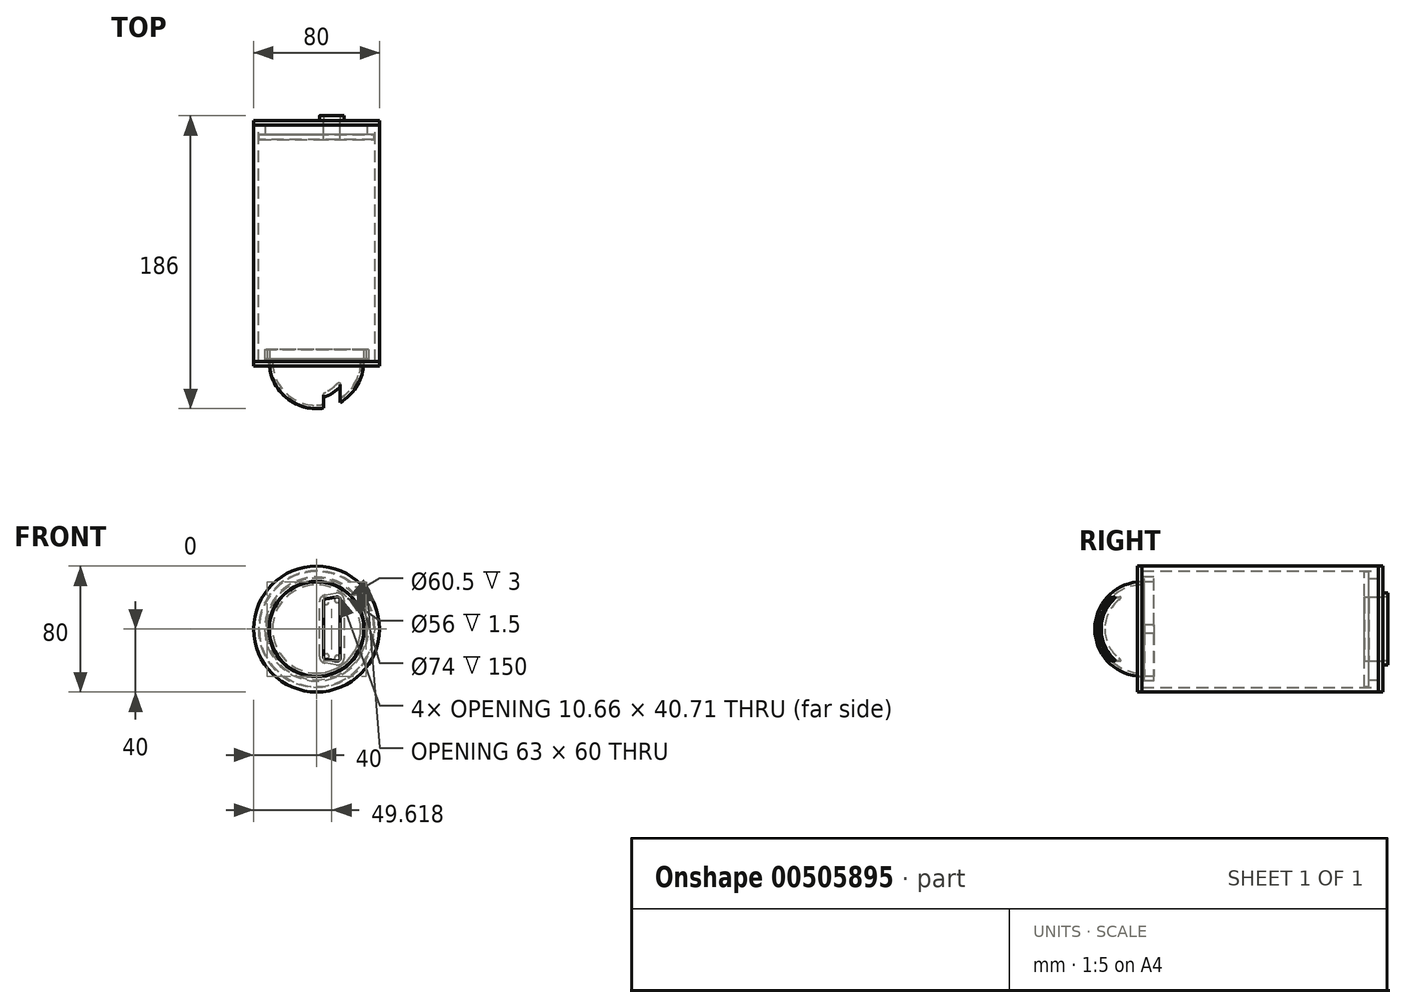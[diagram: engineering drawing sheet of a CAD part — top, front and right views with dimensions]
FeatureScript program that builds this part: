
annotation { "Feature Type Name" : "Feature", "Feature Type Description" : "" }
export const myFeature = defineFeature(function(context is Context, id is Id, definition is map)
    precondition{}
    {
        {
            var Q0;
            Q0=qCreatedBy(makeId("Front.planeOp"),FACE);
            var sketch = newSketch(context, id + "F0", { "sketchPlane" : qUnion([Q0])});
            skCircle(sketch, "E0", {"center": v(0, 0) * mm, "radius": 40 * mm});
            skCircle(sketch, "E1", {"center": v(0, 0) * mm, "radius": 37 * mm});
            skSolve(sketch);
        }
        {
            var Q0;
            Q0 = qSketchRegion(id + "F0", true);
            extrude(context, id + "F1", {"entities" : qUnion([Q0]), "depth" : 150 * mm});
        }
        {
            var Q0;
            Q0=qCreatedBy(makeId("Top.planeOp"),FACE);
            var sketch = newSketch(context, id + "F2", { "sketchPlane" : qUnion([Q0])});
            skArc(sketch, "E2", {"start": v(30, -150) * mm, "mid": v(21.21, -171.21) * mm, "end": v(0, -180) * mm});
            skArc(sketch, "E3.0", {"start": v(28, -150) * mm, "mid": v(19.8, -169.8) * mm, "end": v(0, -178) * mm});
            skLineSegment(sketch, "E4", {"start": v(0, -180) * mm, "end": v(0, -178) * mm});
            skLineSegment(sketch, "E5", {"start": v(30, -150) * mm, "end": v(33, -150) * mm});
            skLineSegment(sketch, "E6", {"start": v(33, -150) * mm, "end": v(33, -148.5) * mm});
            skLineSegment(sketch, "E7", {"start": v(33, -148.5) * mm, "end": v(28, -148.5) * mm});
            skLineSegment(sketch, "E8", {"start": v(28, -148.5) * mm, "end": v(28, -150) * mm});
            skSolve(sketch);
        }
        {
            var Q0;
            Q0 = qSketchRegion(id + "F2", true);
            var Q1;
            Q1=sQuery(id+"F2.wireOp",EDGE,"E4");
            revolve(context, id + "F3", {"entities" : qUnion([Q0]), "axis" : qUnion([Q1]), "revolveType" : RevolveType.FULL});
        }
        {
            var Q0;
            Q0=makeQuery(id+"F1.opExtrude","CAP_FACE",FACE,{"disambiguationData":[OSD([sQuery(id+"F0.wireOp",EDGE,"E0"),sQuery(id+"F0.wireOp",EDGE,"E1")])],"isStart":false});
            var sketch = newSketch(context, id + "F4", { "sketchPlane" : qUnion([Q0])});
            skCircle(sketch, "E9.0", {"center": v(0, 0) * mm, "radius": 40 * mm});
            skCircle(sketch, "E10", {"center": v(0, 0) * mm, "radius": 30.25 * mm});
            skSolve(sketch);
        }
        {
            var Q0;
            Q0 = qSketchRegion(id + "F4", true);
            extrude(context, id + "F5", {"entities" : qUnion([Q0]), "depth" : 3 * mm});
        }
        {
            var Q0;
            Q0=makeQuery(id+"F3.opRevolve","SWEPT_FACE",FACE,{"disambiguationData":[OSD([sQuery(id+"F2.wireOp",EDGE,"E7")])]});
            var sketch = newSketch(context, id + "F6", { "sketchPlane" : qUnion([Q0])});
            skCircle(sketch, "E11.0", {"center": v(0, 0) * mm, "radius": 33 * mm});
            skCircle(sketch, "E12.0", {"center": v(0, 0) * mm, "radius": 30 * mm});
            skCircle(sketch, "E13", {"center": v(-28.5, 0) * mm, "radius": 3 * mm});
            skCircle(sketch, "E14", {"center": v(28.5, 0) * mm, "radius": 3 * mm});
            skSolve(sketch);
        }
        {
            var Q0;
            Q0=makeQuery(id+"F6.imprint","IMPRINT",FACE,{"disambiguationData":[TD([[makeQuery(id+"F6.imprint","IMPRINT",EDGE,{"derivedFrom":sQuery(id+"F6.wireOp",EDGE,"E11.0")}),-1.0]])]});
            extrude(context, id + "F7", {"entities" : qUnion([Q0]), "depth" : 6 * mm});
        }
        {
            var Q0;
            Q0=makeQuery(id+"F1.opExtrude","CAP_FACE",FACE,{"disambiguationData":[OSD([sQuery(id+"F0.wireOp",EDGE,"E0"),sQuery(id+"F0.wireOp",EDGE,"E1")])],"isStart":true});
            var sketch = newSketch(context, id + "F8", { "sketchPlane" : qUnion([Q0])});
            skCircle(sketch, "E15.0", {"center": v(0, 0) * mm, "radius": 40 * mm});
            skSolve(sketch);
        }
        {
            var Q0;
            Q0 = qSketchRegion(id + "F8", true);
            extrude(context, id + "F9", {"entities" : qUnion([Q0]), "depth" : 3 * mm});
        }
        {
            var Q0;
            Q0=makeQuery(id+"F9.opExtrude","CAP_FACE",FACE,{"disambiguationData":[OSD([sQuery(id+"F8.wireOp",EDGE,"E15.0")])],"isStart":true});
            var sketch = newSketch(context, id + "F10", { "sketchPlane" : qUnion([Q0])});
            skCircle(sketch, "E16", {"center": v(0, 0) * mm, "radius": 32.25 * mm});
            skSolve(sketch);
        }
        {
            var Q0;
            Q0 = qSketchRegion(id + "F10", true);
            extrude(context, id + "F11", {"entities" : qUnion([Q0]), "depth" : 6 * mm});
        }
        {
            var Q0;
            Q0=makeQuery(id+"F11.opExtrude","CAP_FACE",FACE,{"disambiguationData":[OSD([sQuery(id+"F10.wireOp",EDGE,"E16")])],"isStart":false});
            var sketch = newSketch(context, id + "F12", { "sketchPlane" : qUnion([Q0])});
            skCircle(sketch, "E17", {"center": v(0, 0) * mm, "radius": 36.5 * mm});
            skSolve(sketch);
        }
        {
            var Q0;
            Q0 = qSketchRegion(id + "F12", true);
            extrude(context, id + "F13", {"entities" : qUnion([Q0]), "depth" : 3 * mm});
        }
        {
            var Q0;
            Q0=makeQuery(id+"F9.opExtrude","CAP_FACE",FACE,{"disambiguationData":[OSD([sQuery(id+"F8.wireOp",EDGE,"E15.0")])],"isStart":false});
            var sketch = newSketch(context, id + "F14", { "sketchPlane" : qUnion([Q0])});
            skLineSegment(sketch, "E18", {"start": v(-12.8, -20.83) * mm, "end": v(-5.71, -19.69) * mm, "construction": true});
            skLineSegment(sketch, "E19", {"start": v(-3.79, -17.43) * mm, "end": v(-3.79, 17.43) * mm, "construction": true});
            skLineSegment(sketch, "E20", {"start": v(-5.71, 19.69) * mm, "end": v(-12.8, 20.83) * mm, "construction": true});
            skLineSegment(sketch, "E21", {"start": v(-15.45, 18.57) * mm, "end": v(-15.45, -18.57) * mm, "construction": true});
            skLineSegment(sketch, "E22", {"start": v(-9.62, -20.32) * mm, "end": v(-9.62, 20.32) * mm, "construction": true});
            skLineSegment(sketch, "E23", {"start": v(-15.45, 0) * mm, "end": v(-3.79, 0) * mm, "construction": true});
            skPoint(sketch, "E24.visualSharp", {"position": v(-15.45, -21.26) * mm});
            skArc(sketch, "E24.filletArc", {"start": v(-15.45, -18.57) * mm, "mid": v(-14.64, -20.31) * mm, "end": v(-12.8, -20.83) * mm, "construction": true});
            skPoint(sketch, "E25.visualSharp", {"position": v(-3.79, -19.38) * mm});
            skArc(sketch, "E25.filletArc", {"start": v(-5.71, -19.69) * mm, "mid": v(-4.33, -18.92) * mm, "end": v(-3.79, -17.43) * mm, "construction": true});
            skPoint(sketch, "E26.visualSharp", {"position": v(-3.79, 19.38) * mm});
            skArc(sketch, "E26.filletArc", {"start": v(-3.79, 17.43) * mm, "mid": v(-4.33, 18.92) * mm, "end": v(-5.71, 19.69) * mm, "construction": true});
            skPoint(sketch, "E27.visualSharp", {"position": v(-15.45, 21.26) * mm});
            skArc(sketch, "E27.filletArc", {"start": v(-12.8, 20.83) * mm, "mid": v(-14.64, 20.31) * mm, "end": v(-15.45, 18.57) * mm, "construction": true});
            skArc(sketch, "E28.0", {"start": v(-12.88, 20.34) * mm, "mid": v(-14.32, 19.93) * mm, "end": v(-14.95, 18.57) * mm});
            skLineSegment(sketch, "E28.1", {"start": v(-5.8, 19.2) * mm, "end": v(-12.88, 20.34) * mm});
            skLineSegment(sketch, "E28.2", {"start": v(-14.95, 18.57) * mm, "end": v(-14.95, -18.57) * mm});
            skArc(sketch, "E28.3", {"start": v(-4.29, 17.43) * mm, "mid": v(-4.72, 18.6) * mm, "end": v(-5.8, 19.2) * mm});
            skArc(sketch, "E28.4", {"start": v(-14.95, -18.57) * mm, "mid": v(-14.32, -19.93) * mm, "end": v(-12.88, -20.34) * mm});
            skLineSegment(sketch, "E28.5", {"start": v(-12.88, -20.34) * mm, "end": v(-5.8, -19.2) * mm});
            skArc(sketch, "E28.6", {"start": v(-5.8, -19.2) * mm, "mid": v(-4.72, -18.6) * mm, "end": v(-4.29, -17.43) * mm});
            skLineSegment(sketch, "E28.7", {"start": v(-4.29, -17.43) * mm, "end": v(-4.29, 17.43) * mm});
            skSolve(sketch);
        }
        {
            var Q0;
            Q0 = qSketchRegion(id + "F14", true);
            extrude(context, id + "F15", {"entities" : qUnion([Q0]), "operationType" : NewBodyOperationType.REMOVE, "endBound" : BoundingType.THROUGH_ALL, "oppositeDirection" : true, "depth" : 25 * mm});
        }
        {
            var Q0;
            Q0=makeQuery(id+"F9.opExtrude","CAP_FACE",FACE,{"disambiguationData":[OSD([sQuery(id+"F8.wireOp",EDGE,"E15.0")])],"isStart":false});
            var sketch = newSketch(context, id + "F16", { "sketchPlane" : qUnion([Q0])});
            skLineSegment(sketch, "E29.0", {"start": v(-14.95, 18.57) * mm, "end": v(-14.95, -18.57) * mm});
            skArc(sketch, "E29.1", {"start": v(-14.95, -18.57) * mm, "mid": v(-14.32, -19.93) * mm, "end": v(-12.88, -20.34) * mm});
            skLineSegment(sketch, "E29.2", {"start": v(-12.88, -20.34) * mm, "end": v(-5.8, -19.2) * mm});
            skArc(sketch, "E29.3", {"start": v(-5.8, -19.2) * mm, "mid": v(-4.72, -18.6) * mm, "end": v(-4.29, -17.43) * mm});
            skLineSegment(sketch, "E29.4", {"start": v(-4.29, -17.43) * mm, "end": v(-4.29, 17.43) * mm});
            skArc(sketch, "E29.5", {"start": v(-4.29, 17.43) * mm, "mid": v(-4.72, 18.6) * mm, "end": v(-5.8, 19.2) * mm});
            skLineSegment(sketch, "E29.6", {"start": v(-5.8, 19.2) * mm, "end": v(-12.88, 20.34) * mm});
            skArc(sketch, "E29.7", {"start": v(-12.88, 20.34) * mm, "mid": v(-14.32, 19.93) * mm, "end": v(-14.95, 18.57) * mm});
            skArc(sketch, "E30.0", {"start": v(-12.48, 22.8) * mm, "mid": v(-15.94, 21.84) * mm, "end": v(-17.45, 18.57) * mm});
            skLineSegment(sketch, "E30.1", {"start": v(-5.4, 21.66) * mm, "end": v(-12.48, 22.8) * mm});
            skLineSegment(sketch, "E30.2", {"start": v(-17.45, 18.57) * mm, "end": v(-17.45, -18.57) * mm});
            skArc(sketch, "E30.3", {"start": v(-1.79, 17.43) * mm, "mid": v(-2.81, 20.21) * mm, "end": v(-5.4, 21.66) * mm});
            skArc(sketch, "E30.4", {"start": v(-17.45, -18.57) * mm, "mid": v(-15.94, -21.84) * mm, "end": v(-12.48, -22.8) * mm});
            skLineSegment(sketch, "E30.5", {"start": v(-12.48, -22.8) * mm, "end": v(-5.4, -21.66) * mm});
            skArc(sketch, "E30.6", {"start": v(-5.4, -21.66) * mm, "mid": v(-2.81, -20.21) * mm, "end": v(-1.79, -17.43) * mm});
            skLineSegment(sketch, "E30.7", {"start": v(-1.79, -17.43) * mm, "end": v(-1.79, 17.43) * mm});
            skSolve(sketch);
        }
        {
            var Q0;
            Q0 = qSketchRegion(id + "F16", true);
            extrude(context, id + "F17", {"entities" : qUnion([Q0]), "depth" : 3 * mm, "offsetDistance" : 25 * mm});
        }
    });
